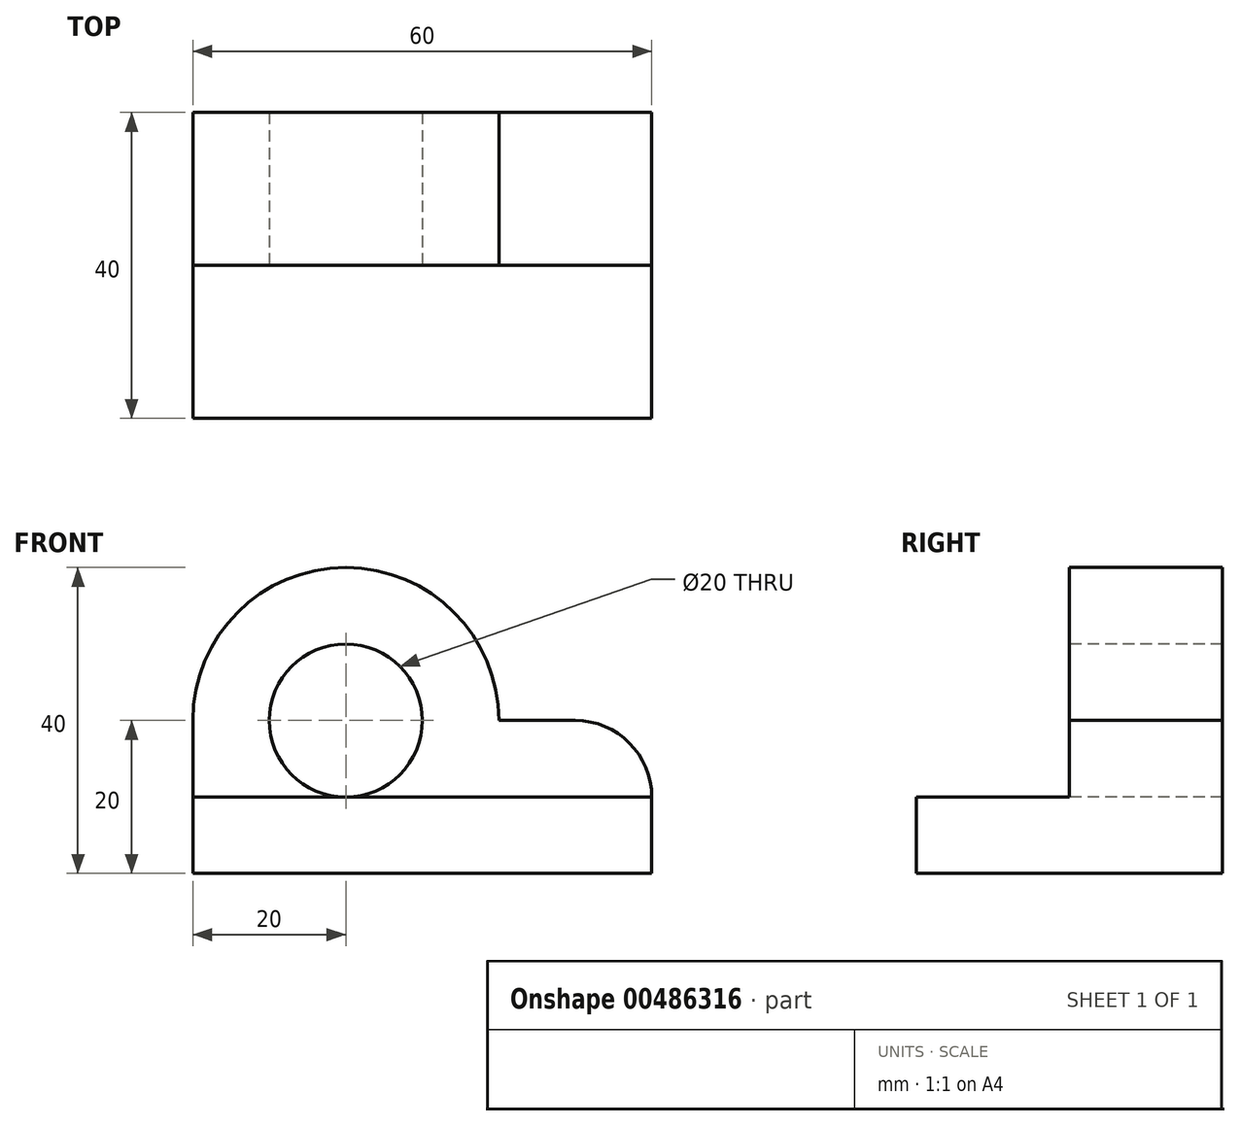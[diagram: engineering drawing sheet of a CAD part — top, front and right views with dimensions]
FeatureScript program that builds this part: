
annotation { "Feature Type Name" : "Feature", "Feature Type Description" : "" }
export const myFeature = defineFeature(function(context is Context, id is Id, definition is map)
    precondition{}
    {
        {
            var Q0;
            Q0=qCreatedBy(makeId("Top.planeOp"),FACE);
            var sketch = newSketch(context, id + "F0", { "sketchPlane" : qUnion([Q0])});
            skLineSegment(sketch, "E0", {"start": v(0, 0) * mm, "end": v(60, 0) * mm});
            skLineSegment(sketch, "E1", {"start": v(60, 0) * mm, "end": v(60, 40) * mm});
            skLineSegment(sketch, "E2", {"start": v(0, 0) * mm, "end": v(0, 40) * mm});
            skLineSegment(sketch, "E3", {"start": v(0, 40) * mm, "end": v(60, 40) * mm});
            skSolve(sketch);
        }
        {
            var Q0;
            Q0=makeQuery(id+"F0.imprint","IMPRINT",FACE,{"disambiguationData":[TD([[makeQuery(id+"F0.imprint","IMPRINT",EDGE,{"derivedFrom":sQuery(id+"F0.wireOp",EDGE,"E0")}),1.0]])]});
            extrude(context, id + "F1", {"entities" : qUnion([Q0]), "depth" : 10 * mm, "offsetDistance" : 25 * mm});
        }
        {
            var Q0;
            Q0=makeQuery(id+"F1.opExtrude","SWEPT_FACE",FACE,{"disambiguationData":[OSD([sQuery(id+"F0.wireOp",EDGE,"E3")])]});
            var sketch = newSketch(context, id + "F2", { "sketchPlane" : qUnion([Q0])});
            skPoint(sketch, "E4", {"position": v(-20, 20) * mm});
            skArc(sketch, "E5", {"start": v(0, 20) * mm, "mid": v(-20, 40) * mm, "end": v(-40, 20) * mm});
            skLineSegment(sketch, "E6", {"start": v(0, 20) * mm, "end": v(0, 10) * mm});
            skLineSegment(sketch, "E7", {"start": v(-40, 20) * mm, "end": v(-50, 20) * mm});
            skLineSegment(sketch, "E8", {"start": v(-60, 10) * mm, "end": v(-60, 10) * mm});
            skPoint(sketch, "E9.visualSharp", {"position": v(-60, 20) * mm});
            skArc(sketch, "E9.filletArc", {"start": v(-50, 20) * mm, "mid": v(-57.07, 17.07) * mm, "end": v(-60, 10) * mm});
            skLineSegment(sketch, "E10", {"start": v(-60, 10) * mm, "end": v(0, 10) * mm});
            skSolve(sketch);
        }
        {
            var Q0;
            Q0 = qSketchRegion(id + "F2", true);
            extrude(context, id + "F3", {"entities" : qUnion([Q0]), "operationType" : NewBodyOperationType.ADD, "oppositeDirection" : true, "depth" : 20 * mm, "offsetDistance" : 25 * mm});
        }
        {
            var Q0;
            Q0=makeQuery(id+"F3.opExtrude","CAP_FACE",FACE,{"disambiguationData":[OSD([sQuery(id+"F2.wireOp",EDGE,"E5"),sQuery(id+"F2.wireOp",EDGE,"E6"),sQuery(id+"F2.wireOp",EDGE,"E7"),sQuery(id+"F2.wireOp",EDGE,"E9.filletArc"),sQuery(id+"F2.wireOp",EDGE,"E10")])],"isStart":false});
            var sketch = newSketch(context, id + "F4", { "sketchPlane" : qUnion([Q0])});
            skCircle(sketch, "E11", {"center": v(20, 20) * mm, "radius": 10 * mm});
            skSolve(sketch);
        }
        {
            var Q0;
            Q0 = qSketchRegion(id + "F4", true);
            extrude(context, id + "F5", {"entities" : qUnion([Q0]), "operationType" : NewBodyOperationType.REMOVE, "oppositeDirection" : true, "depth" : 25 * mm, "offsetDistance" : 25 * mm});
        }
    });
